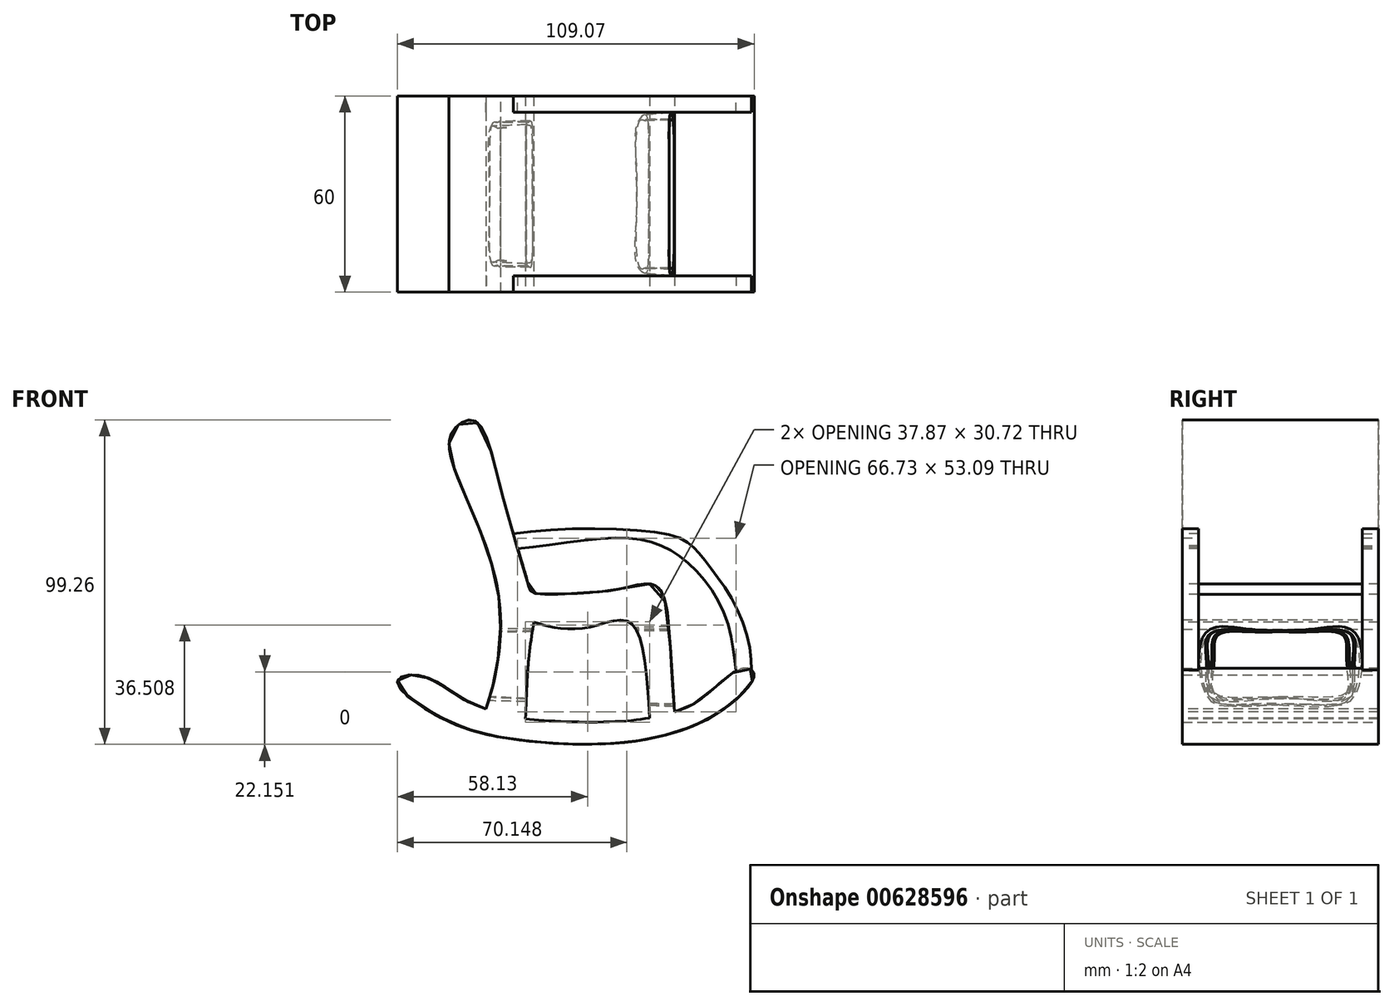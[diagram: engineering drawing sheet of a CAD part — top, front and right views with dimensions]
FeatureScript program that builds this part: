
annotation { "Feature Type Name" : "Feature", "Feature Type Description" : "" }
export const myFeature = defineFeature(function(context is Context, id is Id, definition is map)
    precondition{}
    {
        {
            var Q0;
            Q0=qCreatedBy(makeId("Front.planeOp"),FACE);
            var sketch = newSketch(context, id + "F0", { "sketchPlane" : qUnion([Q0])});
            skFitSpline(sketch, "E0", {"points": [v(-18.42, -38.56) * mm, v(-26.04, -36.93) * mm, v(-36.74, -32.93) * mm, v(-45.82, -27.13) * mm, v(-53.62, -25.13) * mm, v(-57.61, -27.3) * mm, v(-43.28, -38.74) * mm, v(-20.05, -45.1) * mm, v(9.53, -46) * mm, v(31.48, -41.28) * mm, v(44.73, -33.66) * mm, v(51.44, -24.95) * mm, v(48, -23.14) * mm, v(35.82, -32) * mm, v(27.17, -36.4) * mm, v(11.16, -39.28) * mm, v(-18.42, -38.56) * mm]});
            skFitSpline(sketch, "E1", {"points": [v(-30.53, -35.53) * mm, v(-28.03, -26.76) * mm, v(-26.04, -10.8) * mm, v(-28.03, 6.08) * mm, v(-34.93, 25.31) * mm, v(-41.28, 41.46) * mm, v(-40.55, 49.63) * mm, v(-34.2, 52.71) * mm, v(-26.04, 31.84) * mm, v(-17.51, 2.27) * mm, v(-16.06, 0) * mm, v(0, 0) * mm, v(12.25, 1.54) * mm, v(21.68, 1.9) * mm, v(27.17, -36.4) * mm], "startDerivative": vector(47.66, 147.28) * mm, "endDerivative": vector(50.03, -509.91) * mm});
            skFitSpline(sketch, "E2", {"points": [v(-15.88, -8.98) * mm, v(-17.51, -20.78) * mm, v(-18.42, -38.56) * mm], "startDerivative": vector(-4.08, -24.84) * mm, "endDerivative": vector(-1.1, -34) * mm});
            skFitSpline(sketch, "E3", {"points": [v(-15.88, -8.98) * mm, v(-9.7, -10.61) * mm, v(1.72, -10.43) * mm, v(13.34, -8.98) * mm, v(19.46, -38.29) * mm], "startDerivative": vector(33.3, -10.63) * mm, "endDerivative": vector(6.1, -106.87) * mm});
            skSolve(sketch);
        }
        {
            var Q0;
            Q0 = qSketchRegion(id + "F0", true);
            extrude(context, id + "F1", {"entities" : qUnion([Q0]), "depth" : 60 * mm, "offsetDistance" : 25 * mm});
        }
        {
            var Q0;
            {var subQ0=sQuery(id+"F0.wireOp",EDGE,"E2");Q0=makeQuery(id+"F0.imprint","IMPRINT",FACE,{"disambiguationData":[TD([[makeQuery(id+"F0.imprint","IMPRINT",EDGE,{"derivedFrom":subQ0}),1.0]])]});}
            extrude(context, id + "F2", {"entities" : qUnion([Q0]), "operationType" : NewBodyOperationType.REMOVE, "oppositeDirection" : true, "depth" : 25 * mm, "offsetDistance" : 25 * mm});
        }
        {
            var Q0;
            Q0=qCreatedBy(makeId("Right.planeOp"),FACE);
            cPlane(context, id + "F3", {"entities" : qUnion([Q0]), "cplaneType" : CPlaneType.OFFSET, "offset" : 30 * mm, "width" : 150 * mm, "height" : 150 * mm});
        }
        {
            var Q0;
            Q0=qCreatedBy(makeId("Right.planeOp"),FACE);
            cPlane(context, id + "F4", {"entities" : qUnion([Q0]), "cplaneType" : CPlaneType.OFFSET, "offset" : 30 * mm, "oppositeDirection" : true, "width" : 150 * mm, "height" : 150 * mm});
        }
        {
            var Q0;
            Q0=qCreatedBy(id+"F4.planeOp",FACE);
            var sketch = newSketch(context, id + "F5", { "sketchPlane" : qUnion([Q0])});
            skFitSpline(sketch, "E4", {"points": [v(-51.08, -12.61) * mm, v(-51.8, -21.86) * mm, v(-50.9, -30.4) * mm, v(-28.94, -31.84) * mm, v(-10.07, -31.66) * mm, v(-10.07, -20.6) * mm, v(-10.98, -13.16) * mm, v(-26.76, -12.07) * mm, v(-51.08, -12.61) * mm]});
            skSolve(sketch);
        }
        {
            var Q0;
            Q0=qCreatedBy(id+"F3.planeOp",FACE);
            var sketch = newSketch(context, id + "F6", { "sketchPlane" : qUnion([Q0])});
            skFitSpline(sketch, "E5", {"points": [v(-51.62, -12.61) * mm, v(-52.71, -21.14) * mm, v(-50.72, -33.11) * mm, v(-22.23, -34.2) * mm, v(-7.71, -32.39) * mm, v(-6.62, -12.43) * mm, v(-24.77, -11.45) * mm, v(-51.62, -12.61) * mm]});
            skSolve(sketch);
        }
        {
            var Q1;
            Q1=makeQuery(id+"F6.imprint","IMPRINT",FACE,{"disambiguationData":[TD([[makeQuery(id+"F6.imprint","IMPRINT",EDGE,{"derivedFrom":sQuery(id+"F6.wireOp",EDGE,"E5")}),1.0]])]});
            var Q2;
            Q2=makeQuery(id+"F5.imprint","IMPRINT",FACE,{"disambiguationData":[TD([[makeQuery(id+"F5.imprint","IMPRINT",EDGE,{"derivedFrom":sQuery(id+"F5.wireOp",EDGE,"E4")}),1.0]])]});
            loft(context, id + "F7", {"operationType" : NewBodyOperationType.REMOVE, "sheetProfilesArray" : [{ "sheetProfileEntities" : qUnion([Q1]) }, { "sheetProfileEntities" : qUnion([Q2]) }]});
        }
        {
            var Q0;
            Q0=qCreatedBy(makeId("Front.planeOp"),FACE);
            var sketch = newSketch(context, id + "F8", { "sketchPlane" : qUnion([Q0])});
            skFitSpline(sketch, "E6", {"points": [v(49.73, -27.16) * mm, v(47.63, -8.26) * mm, v(35.47, 10.98) * mm, v(24.04, 18.05) * mm, v(-29.3, 15.97) * mm, v(-30.06, 13.6) * mm, v(5.9, 16.6) * mm, v(28.94, 10.98) * mm, v(43.82, -10.8) * mm, v(47.28, -28.05) * mm, v(49.73, -27.16) * mm]});
            skSolve(sketch);
        }
        {
            var Q0;
            Q0 = qSketchRegion(id + "F8", true);
            extrude(context, id + "F9", {"entities" : qUnion([Q0]), "operationType" : NewBodyOperationType.ADD, "depth" : 5 * mm, "offsetDistance" : 25 * mm});
        }
        {
            var Q0;
            Q0=qCreatedBy(makeId("Front.planeOp"),FACE);
            cPlane(context, id + "F10", {"entities" : qUnion([Q0]), "cplaneType" : CPlaneType.OFFSET, "offset" : 30 * mm, "width" : 150 * mm, "height" : 150 * mm});
        }
        {
            var Q0;
            Q0=makeQuery(id+"F1.opExtrude","SWEPT_BODY",BODY,{"disambiguationData":[OSD([sQuery(id+"F0.wireOp",EDGE,"E0"),sQuery(id+"F0.wireOp",EDGE,"E1"),sQuery(id+"F0.wireOp",EDGE,"E2"),sQuery(id+"F0.wireOp",EDGE,"E3")])]});
            var Q1;
            Q1=qCreatedBy(id+"F10.planeOp",FACE);
            mirror(context, id + "F11", {"entities" : qUnion([Q0]), "mirrorPlane" : qUnion([Q1])});
        }
    });
